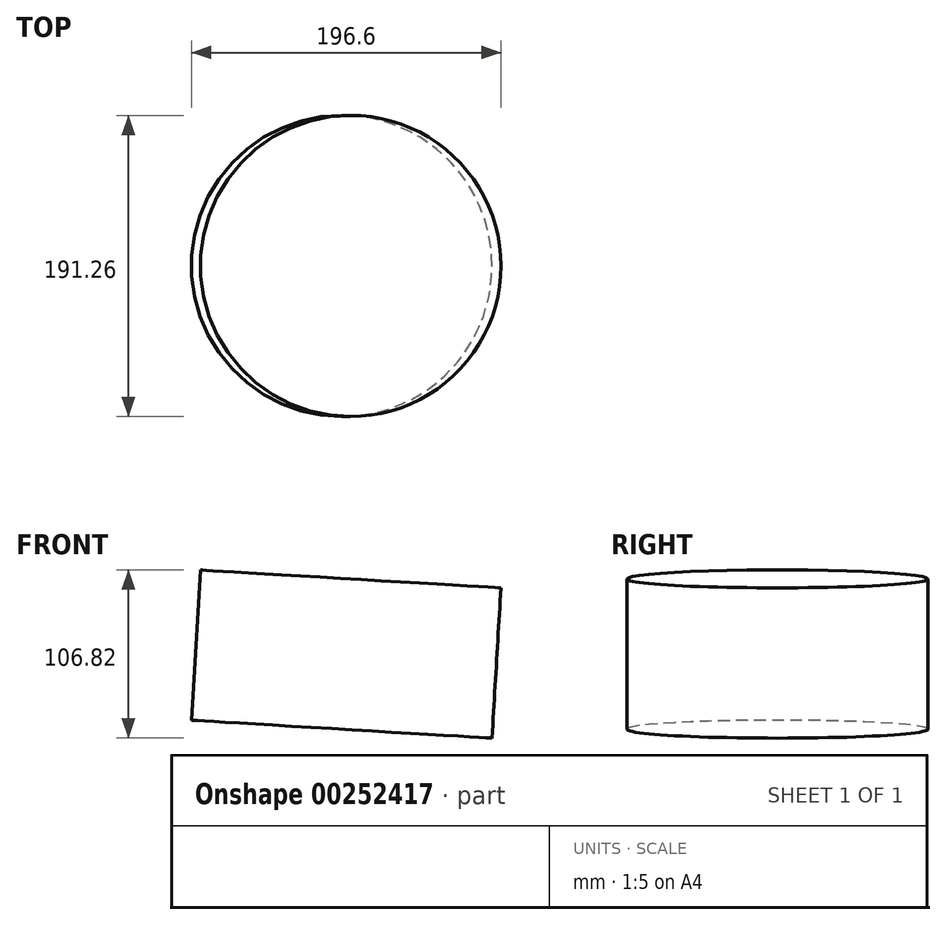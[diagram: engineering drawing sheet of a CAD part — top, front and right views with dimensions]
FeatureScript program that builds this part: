
annotation { "Feature Type Name" : "Feature", "Feature Type Description" : "" }
export const myFeature = defineFeature(function(context is Context, id is Id, definition is map)
    precondition{}
    {
        {
            var Q0;
            Q0=qCreatedBy(makeId("Front.planeOp"),FACE);
            var sketch = newSketch(context, id + "F0", { "sketchPlane" : qUnion([Q0])});
            skCircle(sketch, "E0.cCircle", {"center": v(0, 0) * mm, "radius": 67.62 * mm, "construction": true});
            skLineSegment(sketch, "E0.0", {"start": v(-44.89, 50.57) * mm, "end": v(50.57, 44.89) * mm});
            skLineSegment(sketch, "E0.1", {"start": v(50.57, 44.89) * mm, "end": v(44.89, -50.57) * mm});
            skLineSegment(sketch, "E0.2", {"start": v(44.89, -50.57) * mm, "end": v(-50.57, -44.89) * mm});
            skLineSegment(sketch, "E0.3", {"start": v(-50.57, -44.89) * mm, "end": v(-44.89, 50.57) * mm});
            skSolve(sketch);
        }
        {
            var Q0;
            Q0=makeQuery(id+"F0.imprint","IMPRINT",FACE,{"disambiguationData":[TD([[makeQuery(id+"F0.imprint","IMPRINT",EDGE,{"derivedFrom":sQuery(id+"F0.wireOp",EDGE,"E0.0")}),-1.0]])]});
            var Q1;
            Q1=sQuery(id+"F0.wireOp",EDGE,"E0.1");
            revolve(context, id + "F1", {"entities" : qUnion([Q0]), "axis" : qUnion([Q1]), "revolveType" : RevolveType.FULL});
        }
    });
